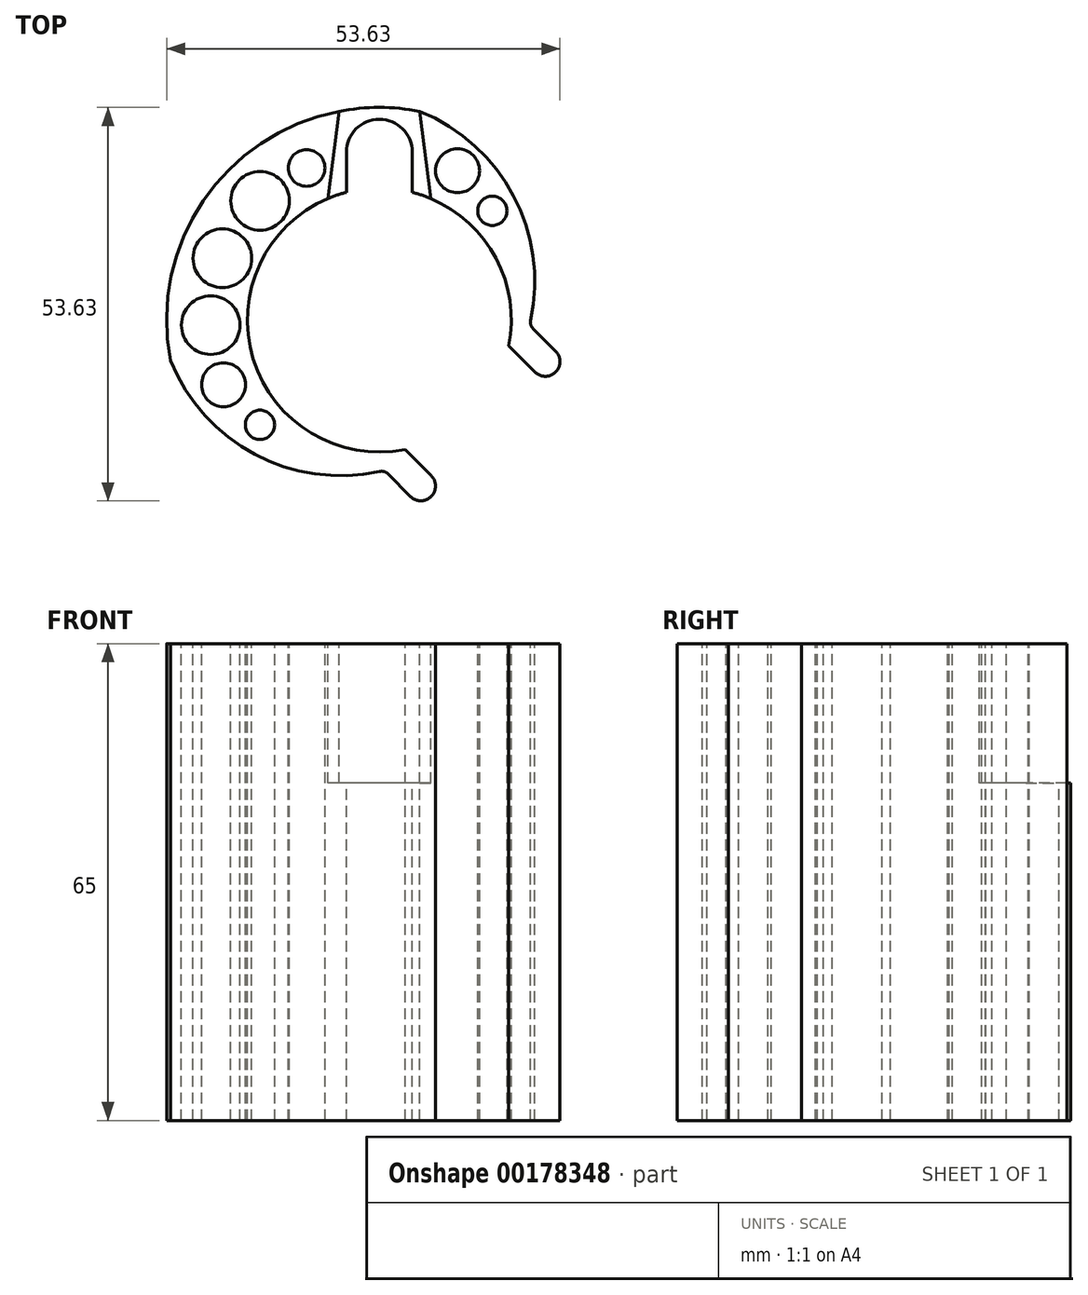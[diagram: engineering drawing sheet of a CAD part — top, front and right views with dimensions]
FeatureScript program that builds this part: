
annotation { "Feature Type Name" : "Feature", "Feature Type Description" : "" }
export const myFeature = defineFeature(function(context is Context, id is Id, definition is map)
    precondition{}
    {
        {
            var Q0;
            Q0=qCreatedBy(makeId("Front.planeOp"),FACE);
            var sketch = newSketch(context, id + "F0", { "sketchPlane" : qUnion([Q0])});
            skLineSegment(sketch, "E0.bottom", {"start": v(-18, 32.5) * mm, "end": v(-29, 32.5) * mm});
            skLineSegment(sketch, "E0.top", {"start": v(-18, -32.5) * mm, "end": v(-29, -32.5) * mm});
            skLineSegment(sketch, "E0.left", {"start": v(-18, 32.5) * mm, "end": v(-18, -32.5) * mm});
            skLineSegment(sketch, "E0.right", {"start": v(-29, 32.5) * mm, "end": v(-29, -32.5) * mm});
            skPoint(sketch, "E1", {"position": v(-18, 0) * mm});
            skLineSegment(sketch, "E2", {"start": v(0, 26.11) * mm, "end": v(0, -24.38) * mm, "construction": true});
            skSolve(sketch);
        }
        {
            var Q0;
            Q0=makeQuery(id+"F0.imprint","IMPRINT",FACE,{"disambiguationData":[TD([[makeQuery(id+"F0.imprint","IMPRINT",EDGE,{"derivedFrom":sQuery(id+"F0.wireOp",EDGE,"E0.bottom")}),1.0]])]});
            var Q1;
            Q1=sQuery(id+"F0.wireOp",EDGE,"E2");
            revolve(context, id + "F1", {"entities" : qUnion([Q0]), "axis" : qUnion([Q1]), "revolveType" : RevolveType.FULL});
        }
        {
            var Q0;
            Q0=makeQuery(id+"F1.opRevolve","SWEPT_FACE",FACE,{"disambiguationData":[OSD([sQuery(id+"F0.wireOp",EDGE,"E0.bottom")])]});
            var sketch = newSketch(context, id + "F2", { "sketchPlane" : qUnion([Q0])});
            skCircle(sketch, "E3", {"center": v(0, 22.9) * mm, "radius": 4.5 * mm});
            skLineSegment(sketch, "E4", {"start": v(4.5, 22.9) * mm, "end": v(4.5, 17.43) * mm});
            skLineSegment(sketch, "E5", {"start": v(-4.5, 22.9) * mm, "end": v(-4.5, 17.43) * mm});
            skLineSegment(sketch, "E6", {"start": v(-5.5, 28.47) * mm, "end": v(5.5, 28.47) * mm});
            skLineSegment(sketch, "E7", {"start": v(-7, 16.58) * mm, "end": v(7, 16.58) * mm});
            skLineSegment(sketch, "E8", {"start": v(-5.5, 28.47) * mm, "end": v(-7, 16.58) * mm});
            skLineSegment(sketch, "E9", {"start": v(5.5, 28.47) * mm, "end": v(7, 16.58) * mm});
            skLineSegment(sketch, "E10.bottom", {"start": v(3.51, -17.65) * mm, "end": v(-6.98, -28.15) * mm});
            skLineSegment(sketch, "E10.top", {"start": v(8.49, -22.63) * mm, "end": v(-2, -33.12) * mm});
            skLineSegment(sketch, "E10.left", {"start": v(3.51, -17.65) * mm, "end": v(8.49, -22.63) * mm});
            skLineSegment(sketch, "E10.right", {"start": v(-6.98, -28.15) * mm, "end": v(-2, -33.12) * mm});
            skLineSegment(sketch, "E11.bottom", {"start": v(17.65, -3.51) * mm, "end": v(28.15, 6.98) * mm});
            skLineSegment(sketch, "E11.top", {"start": v(22.63, -8.49) * mm, "end": v(33.12, 2) * mm});
            skLineSegment(sketch, "E11.left", {"start": v(17.65, -3.51) * mm, "end": v(22.63, -8.49) * mm});
            skLineSegment(sketch, "E11.right", {"start": v(28.15, 6.98) * mm, "end": v(33.12, 2) * mm});
            skLineSegment(sketch, "E12", {"start": v(20.48, -0.68) * mm, "end": v(25.46, -5.66) * mm});
            skLineSegment(sketch, "E13", {"start": v(0.68, -20.48) * mm, "end": v(5.66, -25.46) * mm});
            skLineSegment(sketch, "E14", {"start": v(0, 10.06) * mm, "end": v(0, 36.25) * mm, "construction": true});
            skLineSegment(sketch, "E15", {"start": v(0, 0) * mm, "end": v(32.33, -32.33) * mm, "construction": true});
            skLineSegment(sketch, "E16", {"start": v(0, 0) * mm, "end": v(-47.08, 0) * mm, "construction": true});
            skPoint(sketch, "E17", {"position": v(0, 29) * mm});
            skLineSegment(sketch, "E18", {"start": v(-28.47, 5.5) * mm, "end": v(-28.47, -5.5) * mm});
            skArc(sketch, "E19", {"start": v(20.48, -0.68) * mm, "mid": v(18.44, 16.7) * mm, "end": v(5.5, 28.47) * mm});
            skArc(sketch, "E20", {"start": v(-28.47, -5.5) * mm, "mid": v(-16.7, -18.44) * mm, "end": v(0.68, -20.48) * mm});
            skLineSegment(sketch, "E21", {"start": v(0, 0) * mm, "end": v(-29.09, 29.09) * mm, "construction": true});
            skCircle(sketch, "E22", {"center": v(-16.26, 16.26) * mm, "radius": 4 * mm});
            skCircle(sketch, "E23", {"center": v(0, 0) * mm, "radius": 23 * mm, "construction": true});
            skCircle(sketch, "E24", {"center": v(-21.4, 8.44) * mm, "radius": 4 * mm});
            skCircle(sketch, "E25", {"center": v(-22.99, -0.68) * mm, "radius": 4 * mm});
            skCircle(sketch, "E26", {"center": v(10.66, 20.38) * mm, "radius": 3 * mm});
            skCircle(sketch, "E27", {"center": v(-9.92, 20.75) * mm, "radius": 2.5 * mm});
            skCircle(sketch, "E28", {"center": v(-21.24, -8.81) * mm, "radius": 3 * mm});
            skCircle(sketch, "E29", {"center": v(-16.27, -14.28) * mm, "radius": 2 * mm});
            skCircle(sketch, "E30", {"center": v(15.4, 14.9) * mm, "radius": 2 * mm});
            skSolve(sketch);
        }
        {
            var Q0;
            {var subQ1=sQuery(id+"F2.wireOp",EDGE,"E4");Q0=makeQuery(id+"F2.imprint","IMPRINT",FACE,{"disambiguationData":[TD([[makeQuery(id+"F2.imprint","IMPRINT",EDGE,{"derivedFrom":subQ1}),1.0]])]});}
            var Q1;
            {var subQ0=sQuery(id+"F2.wireOp",EDGE,"E6");Q1=makeQuery(id+"F2.imprint","IMPRINT",FACE,{"disambiguationData":[TD([[makeQuery(id+"F2.imprint","IMPRINT",EDGE,{"derivedFrom":subQ0}),1.0]])]});}
            extrude(context, id + "F3", {"entities" : qUnion([Q0, Q1]), "operationType" : NewBodyOperationType.REMOVE, "oppositeDirection" : true, "depth" : 19 * mm});
        }
        {
            var Q0;
            {var subQ0=sQuery(id+"F2.wireOp",EDGE,"E10.top");Q0=makeQuery(id+"F2.imprint","IMPRINT",FACE,{"disambiguationData":[TD([[makeQuery(id+"F2.imprint","IMPRINT",EDGE,{"derivedFrom":subQ0}),-1.0]])]});}
            var Q1;
            {var subQ0=sQuery(id+"F2.wireOp",EDGE,"E11.top");Q1=makeQuery(id+"F2.imprint","IMPRINT",FACE,{"disambiguationData":[TD([[makeQuery(id+"F2.imprint","IMPRINT",EDGE,{"derivedFrom":subQ0}),1.0]])]});}
            var Q2;
            Q2=makeQuery(id+"F1.opRevolve","SWEPT_FACE",FACE,{"disambiguationData":[OSD([sQuery(id+"F0.wireOp",EDGE,"E0.top")])]});
            extrude(context, id + "F4", {"entities" : qUnion([Q0, Q1]), "operationType" : NewBodyOperationType.ADD, "endBound" : BoundingType.UP_TO_SURFACE, "oppositeDirection" : true, "endBoundEntityFace" : qUnion([Q2]), "depth" : 25 * mm});
        }
        {
            var Q0;
            {var subQ0=sQuery(id+"F2.wireOp",EDGE,"E4");Q0=makeQuery(id+"F2.imprint","IMPRINT",FACE,{"disambiguationData":[TD([[makeQuery(id+"F2.imprint","IMPRINT",EDGE,{"derivedFrom":subQ0}),-1.0]])]});}
            var Q1;
            {var subQ0=sQuery(id+"F2.wireOp",EDGE,"E7");Q1=makeQuery(id+"F2.imprint","IMPRINT",FACE,{"disambiguationData":[TD([[makeQuery(id+"F2.imprint","IMPRINT",EDGE,{"derivedFrom":subQ0}),1.0]])]});}
            var Q2;
            {var subQ0=sQuery(id+"F2.wireOp",EDGE,"E4");Q2=makeQuery(id+"F2.imprint","IMPRINT",FACE,{"disambiguationData":[TD([[makeQuery(id+"F2.imprint","IMPRINT",EDGE,{"derivedFrom":subQ0}),-1.0]])]});}
            var Q3;
            {var subQ0=sQuery(id+"F2.wireOp",EDGE,"E3");var subQ1=makeQuery(id+"F2.imprint","INTERSECT",VERTEX,{"derivedFrom":[subQ0,sQuery(id+"F2.wireOp",EDGE,"E4")]});Q3=makeQuery(id+"F2.imprint","IMPRINT",FACE,{"disambiguationData":[TD([[makeQuery(id+"F2.imprint","IMPRINT",EDGE,{"disambiguationData":[TD([[subQ1,-1.0]])],"derivedFrom":subQ0}),1.0]])]});}
            var Q4;
            {var subQ0=sQuery(id+"F2.wireOp",EDGE,"a1OmJimA-APtN-bGwe-B6tO-11LfKIgSePBn");Q4=makeQuery(id+"F2.imprint","IMPRINT",FACE,{"disambiguationData":[TD([[makeQuery(id+"F2.imprint","IMPRINT",EDGE,{"derivedFrom":subQ0}),-1.0]])]});}
            var Q5;
            {var subQ0=sQuery(id+"F2.wireOp",EDGE,"E10.left");var subQ1=sQuery(id+"F0.wireOp",EDGE,"E0.bottom");var subQ4=makeQuery(id+"F1.opRevolve","SWEPT_EDGE",EDGE,{"disambiguationData":[OSD([subQ1,sQuery(id+"F0.wireOp",EDGE,"E0.right")])]});var subQ5=makeQuery(id+"F2.imprint","INTERSECT",VERTEX,{"derivedFrom":[subQ4,subQ0]});Q5=makeQuery(id+"F2.imprint","IMPRINT",FACE,{"disambiguationData":[TD([[makeQuery(id+"F2.imprint","IMPRINT",EDGE,{"disambiguationData":[TD([[subQ5,1.0]])],"derivedFrom":subQ0}),1.0]])]});}
            var Q6;
            {var subQ0=sQuery(id+"F2.wireOp",EDGE,"E10.bottom");var subQ3=sQuery(id+"F2.wireOp",EDGE,"f805bfa0-6c3b-483c-aa07-8e93bd6a3935");var subQ4=makeQuery(id+"F2.imprint","INTERSECT",VERTEX,{"derivedFrom":[subQ0,sQuery(id+"F2.wireOp",EDGE,"E13"),subQ3]});Q6=makeQuery(id+"F2.imprint","IMPRINT",FACE,{"disambiguationData":[TD([[makeQuery(id+"F2.imprint","IMPRINT",EDGE,{"disambiguationData":[TD([[subQ4,1.0]])],"derivedFrom":subQ3}),-1.0]])]});}
            var Q7;
            {var subQ0=sQuery(id+"F2.wireOp",EDGE,"E10.bottom");var subQ3=sQuery(id+"F2.wireOp",EDGE,"E13");var subQ4=makeQuery(id+"F2.imprint","INTERSECT",VERTEX,{"derivedFrom":[subQ0,subQ3,sQuery(id+"F2.wireOp",EDGE,"f805bfa0-6c3b-483c-aa07-8e93bd6a3935")]});Q7=makeQuery(id+"F2.imprint","IMPRINT",FACE,{"disambiguationData":[TD([[makeQuery(id+"F2.imprint","IMPRINT",EDGE,{"disambiguationData":[TD([[subQ4,-1.0]])],"derivedFrom":subQ3}),-1.0]])]});}
            var Q8;
            {var subQ0=sQuery(id+"F2.wireOp",EDGE,"E11.bottom");var subQ3=sQuery(id+"F2.wireOp",EDGE,"E12");var subQ4=makeQuery(id+"F2.imprint","INTERSECT",VERTEX,{"derivedFrom":[subQ0,subQ3,sQuery(id+"F2.wireOp",EDGE,"a9218696-1b7a-4d31-9a07-934ffbfcfd7e")]});Q8=makeQuery(id+"F2.imprint","IMPRINT",FACE,{"disambiguationData":[TD([[makeQuery(id+"F2.imprint","IMPRINT",EDGE,{"disambiguationData":[TD([[subQ4,-1.0]])],"derivedFrom":subQ3}),1.0]])]});}
            var Q9;
            {var subQ3=sQuery(id+"F2.wireOp",EDGE,"a9218696-1b7a-4d31-9a07-934ffbfcfd7e");Q9=makeQuery(id+"F2.imprint","IMPRINT",FACE,{"disambiguationData":[TD([[makeQuery(id+"F2.imprint","IMPRINT",EDGE,{"derivedFrom":subQ3}),1.0]])]});}
            var Q10;
            {var subQ0=sQuery(id+"F2.wireOp",EDGE,"f805bfa0-6c3b-483c-aa07-8e93bd6a3935");var subQ1=makeQuery(id+"F1.opRevolve","SWEPT_EDGE",EDGE,{"disambiguationData":[OSD([sQuery(id+"F0.wireOp",EDGE,"E0.bottom"),sQuery(id+"F0.wireOp",EDGE,"E0.right")])]});var subQ3=makeQuery(id+"F2.imprint","INTERSECT",VERTEX,{"disambiguationData":[OD(0.0)],"derivedFrom":[subQ1,subQ0]});Q10=makeQuery(id+"F2.imprint","IMPRINT",FACE,{"disambiguationData":[TD([[makeQuery(id+"F2.imprint","IMPRINT",EDGE,{"disambiguationData":[TD([[subQ3,1.0]])],"derivedFrom":subQ0}),-1.0]])]});}
            var Q11;
            {var subQ0=sQuery(id+"F2.wireOp",EDGE,"E10.right");Q11=makeQuery(id+"F2.imprint","IMPRINT",FACE,{"disambiguationData":[TD([[makeQuery(id+"F2.imprint","IMPRINT",EDGE,{"derivedFrom":subQ0}),1.0]])]});}
            var Q12;
            {var subQ0=sQuery(id+"F2.wireOp",EDGE,"E11.right");Q12=makeQuery(id+"F2.imprint","IMPRINT",FACE,{"disambiguationData":[TD([[makeQuery(id+"F2.imprint","IMPRINT",EDGE,{"derivedFrom":subQ0}),-1.0]])]});}
            var Q13;
            {var subQ3=sQuery(id+"F2.wireOp",EDGE,"E19");Q13=makeQuery(id+"F2.imprint","IMPRINT",FACE,{"disambiguationData":[TD([[makeQuery(id+"F2.imprint","IMPRINT",EDGE,{"derivedFrom":subQ3}),-1.0]])]});}
            var Q14;
            {var subQ3=sQuery(id+"F2.wireOp",EDGE,"E20");Q14=makeQuery(id+"F2.imprint","IMPRINT",FACE,{"disambiguationData":[TD([[makeQuery(id+"F2.imprint","IMPRINT",EDGE,{"derivedFrom":subQ3}),-1.0]])]});}
            extrude(context, id + "F5", {"entities" : qUnion([Q0, Q1, Q2, Q3, Q4, Q5, Q6, Q7, Q8, Q9, Q10, Q11, Q12, Q13, Q14]), "operationType" : NewBodyOperationType.REMOVE, "endBound" : BoundingType.THROUGH_ALL, "oppositeDirection" : true, "depth" : 25 * mm});
        }
        {
            var Q0;
            Q0=makeQuery(id+"F4.opExtrude","SWEPT_EDGE",EDGE,{"disambiguationData":[OSD([sQuery(id+"F2.wireOp",EDGE,"E10.top"),sQuery(id+"F2.wireOp",EDGE,"E10.right")])]});
            var Q1;
            Q1=makeQuery(id+"F4.opExtrude","SWEPT_EDGE",EDGE,{"disambiguationData":[OSD([sQuery(id+"F2.wireOp",EDGE,"E11.top"),sQuery(id+"F2.wireOp",EDGE,"E11.right")])]});
            var Q2;
            Q2=makeQuery(id+"F5.boolean.opBoolean","COPY",EDGE,{"derivedFrom":makeQuery(id+"F5.opExtrude","SWEPT_EDGE",EDGE,{"disambiguationData":[OSD([sQuery(id+"F0.wireOp",EDGE,"E0.bottom"),sQuery(id+"F0.wireOp",EDGE,"E0.left"),sQuery(id+"F2.wireOp",EDGE,"E10.bottom"),sQuery(id+"F2.wireOp",EDGE,"E10.left")])]})});
            var Q3;
            Q3=makeQuery(id+"F5.boolean.opBoolean","COPY",EDGE,{"derivedFrom":makeQuery(id+"F5.opExtrude","SWEPT_EDGE",EDGE,{"disambiguationData":[OSD([sQuery(id+"F0.wireOp",EDGE,"E0.bottom"),sQuery(id+"F0.wireOp",EDGE,"E0.left"),sQuery(id+"F2.wireOp",EDGE,"E4")])]})});
            var Q4;
            Q4=makeQuery(id+"F3.boolean.opBoolean","COPY",EDGE,{"derivedFrom":makeQuery(id+"F3.opExtrude","SWEPT_EDGE",EDGE,{"disambiguationData":[OSD([sQuery(id+"F0.wireOp",EDGE,"E0.bottom"),sQuery(id+"F0.wireOp",EDGE,"E0.left"),sQuery(id+"F2.wireOp",EDGE,"E7"),sQuery(id+"F2.wireOp",EDGE,"E9")])]})});
            var Q5;
            Q5=makeQuery(id+"F3.boolean.opBoolean","COPY",EDGE,{"derivedFrom":makeQuery(id+"F3.opExtrude","SWEPT_EDGE",EDGE,{"disambiguationData":[OSD([sQuery(id+"F0.wireOp",EDGE,"E0.bottom"),sQuery(id+"F0.wireOp",EDGE,"E0.left"),sQuery(id+"F2.wireOp",EDGE,"E7"),sQuery(id+"F2.wireOp",EDGE,"E8")])]})});
            var Q6;
            Q6=makeQuery(id+"F5.boolean.opBoolean","COPY",EDGE,{"derivedFrom":makeQuery(id+"F5.opExtrude","SWEPT_EDGE",EDGE,{"disambiguationData":[OSD([sQuery(id+"F0.wireOp",EDGE,"E0.bottom"),sQuery(id+"F0.wireOp",EDGE,"E0.left"),sQuery(id+"F2.wireOp",EDGE,"E5")])]})});
            var Q7;
            Q7=makeQuery(id+"F3.boolean.opBoolean","COPY",EDGE,{"derivedFrom":makeQuery(id+"F3.opExtrude","SWEPT_EDGE",EDGE,{"disambiguationData":[OSD([sQuery(id+"F0.wireOp",EDGE,"E0.bottom"),sQuery(id+"F0.wireOp",EDGE,"E0.right"),sQuery(id+"F2.wireOp",EDGE,"E6"),sQuery(id+"F2.wireOp",EDGE,"E9")])]})});
            var Q8;
            Q8=makeQuery(id+"F3.boolean.opBoolean","COPY",EDGE,{"derivedFrom":makeQuery(id+"F3.opExtrude","SWEPT_EDGE",EDGE,{"disambiguationData":[OSD([sQuery(id+"F0.wireOp",EDGE,"E0.bottom"),sQuery(id+"F0.wireOp",EDGE,"E0.right"),sQuery(id+"F2.wireOp",EDGE,"E6"),sQuery(id+"F2.wireOp",EDGE,"E8")])]})});
            var Q9;
            Q9=makeQuery(id+"F5.boolean.opBoolean","COPY",EDGE,{"derivedFrom":makeQuery(id+"F5.opExtrude","SWEPT_EDGE",EDGE,{"disambiguationData":[OSD([sQuery(id+"F2.wireOp",EDGE,"E10.bottom"),sQuery(id+"F2.wireOp",EDGE,"E13"),sQuery(id+"F2.wireOp",EDGE,"f805bfa0-6c3b-483c-aa07-8e93bd6a3935")])]})});
            var Q10;
            Q10=makeQuery(id+"F5.boolean.opBoolean","COPY",EDGE,{"derivedFrom":makeQuery(id+"F5.opExtrude","SWEPT_EDGE",EDGE,{"disambiguationData":[OSD([sQuery(id+"F2.wireOp",EDGE,"E11.bottom"),sQuery(id+"F2.wireOp",EDGE,"E12"),sQuery(id+"F2.wireOp",EDGE,"a9218696-1b7a-4d31-9a07-934ffbfcfd7e")])]})});
            var Q11;
            Q11=makeQuery(id+"F5.boolean.opBoolean","COPY",EDGE,{"derivedFrom":makeQuery(id+"F5.opExtrude","SWEPT_EDGE",EDGE,{"disambiguationData":[OSD([sQuery(id+"F0.wireOp",EDGE,"E0.bottom"),sQuery(id+"F0.wireOp",EDGE,"E0.left"),sQuery(id+"F2.wireOp",EDGE,"E11.bottom"),sQuery(id+"F2.wireOp",EDGE,"E11.left")])]})});
            fillet(context, id + "F6", {"entities" : qUnion([Q0, Q1, Q2, Q3, Q4, Q5, Q6, Q7, Q8, Q9, Q10, Q11]), "radius" : 1.2 * mm, "tangentPropagation" : true, "allowEdgeOverflow" : false});
        }
        {
            var Q0;
            Q0=makeQuery(id+"F5.boolean.opBoolean","COPY",EDGE,{"derivedFrom":makeQuery(id+"F5.opExtrude","SWEPT_EDGE",EDGE,{"disambiguationData":[OSD([sQuery(id+"F2.wireOp",EDGE,"E10.top"),sQuery(id+"F2.wireOp",EDGE,"E13")])]})});
            var Q1;
            Q1=makeQuery(id+"F4.opExtrude","SWEPT_EDGE",EDGE,{"disambiguationData":[OSD([sQuery(id+"F2.wireOp",EDGE,"E10.top"),sQuery(id+"F2.wireOp",EDGE,"E10.left")])]});
            var Q2;
            Q2=makeQuery(id+"F4.opExtrude","SWEPT_EDGE",EDGE,{"disambiguationData":[OSD([sQuery(id+"F2.wireOp",EDGE,"E11.top"),sQuery(id+"F2.wireOp",EDGE,"E11.left")])]});
            var Q3;
            Q3=makeQuery(id+"F5.boolean.opBoolean","COPY",EDGE,{"derivedFrom":makeQuery(id+"F5.opExtrude","SWEPT_EDGE",EDGE,{"disambiguationData":[OSD([sQuery(id+"F2.wireOp",EDGE,"E11.top"),sQuery(id+"F2.wireOp",EDGE,"E12")])]})});
            var Q4;
            Q4=makeQuery(id+"F5.boolean.opBoolean","COPY",EDGE,{"derivedFrom":makeQuery(id+"F5.opExtrude","SWEPT_EDGE",EDGE,{"disambiguationData":[OSD([sQuery(id+"F2.wireOp",EDGE,"E10.top"),sQuery(id+"F2.wireOp",EDGE,"E10.left")])]})});
            var Q5;
            Q5=makeQuery(id+"F5.boolean.opBoolean","COPY",EDGE,{"derivedFrom":makeQuery(id+"F5.opExtrude","SWEPT_EDGE",EDGE,{"disambiguationData":[OSD([sQuery(id+"F2.wireOp",EDGE,"E11.top"),sQuery(id+"F2.wireOp",EDGE,"E11.left")])]})});
            fillet(context, id + "F7", {"entities" : qUnion([Q0, Q1, Q2, Q3, Q4, Q5]), "radius" : 2 * mm, "tangentPropagation" : true, "allowEdgeOverflow" : false});
        }
        {
            var Q0;
            Q0=makeQuery(id+"F2.imprint","IMPRINT",FACE,{"disambiguationData":[TD([[makeQuery(id+"F2.imprint","IMPRINT",EDGE,{"derivedFrom":sQuery(id+"F2.wireOp",EDGE,"E27")}),1.0]])]});
            var Q1;
            Q1=makeQuery(id+"F2.imprint","IMPRINT",FACE,{"disambiguationData":[TD([[makeQuery(id+"F2.imprint","IMPRINT",EDGE,{"derivedFrom":sQuery(id+"F2.wireOp",EDGE,"E22")}),1.0]])]});
            var Q2;
            Q2=makeQuery(id+"F2.imprint","IMPRINT",FACE,{"disambiguationData":[TD([[makeQuery(id+"F2.imprint","IMPRINT",EDGE,{"derivedFrom":sQuery(id+"F2.wireOp",EDGE,"E24")}),1.0]])]});
            var Q3;
            Q3=makeQuery(id+"F2.imprint","IMPRINT",FACE,{"disambiguationData":[TD([[makeQuery(id+"F2.imprint","IMPRINT",EDGE,{"derivedFrom":sQuery(id+"F2.wireOp",EDGE,"E26")}),1.0]])]});
            var Q4;
            Q4=makeQuery(id+"F2.imprint","IMPRINT",FACE,{"disambiguationData":[TD([[makeQuery(id+"F2.imprint","IMPRINT",EDGE,{"derivedFrom":sQuery(id+"F2.wireOp",EDGE,"E25")}),1.0]])]});
            var Q5;
            Q5=makeQuery(id+"F2.imprint","IMPRINT",FACE,{"disambiguationData":[TD([[makeQuery(id+"F2.imprint","IMPRINT",EDGE,{"derivedFrom":sQuery(id+"F2.wireOp",EDGE,"E28")}),1.0]])]});
            var Q6;
            Q6=makeQuery(id+"F2.imprint","IMPRINT",FACE,{"disambiguationData":[TD([[makeQuery(id+"F2.imprint","IMPRINT",EDGE,{"derivedFrom":sQuery(id+"F2.wireOp",EDGE,"E29")}),1.0]])]});
            var Q7;
            Q7=makeQuery(id+"F2.imprint","IMPRINT",FACE,{"disambiguationData":[TD([[makeQuery(id+"F2.imprint","IMPRINT",EDGE,{"derivedFrom":sQuery(id+"F2.wireOp",EDGE,"E30")}),1.0]])]});
            extrude(context, id + "F8", {"entities" : qUnion([Q0, Q1, Q2, Q3, Q4, Q5, Q6, Q7]), "operationType" : NewBodyOperationType.REMOVE, "endBound" : BoundingType.THROUGH_ALL, "oppositeDirection" : true, "depth" : 25 * mm});
        }
    });
